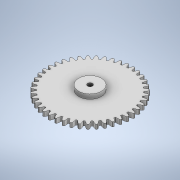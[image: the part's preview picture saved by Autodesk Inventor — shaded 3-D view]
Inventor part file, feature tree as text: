
AUTODESK INVENTOR PART (.ipt)
format: ipt  version: 2020 (Build 240168000, 168)  size: 538,112 bytes
history: native  units: mm
features: sketch x3, extrude x2, fillet x1, pattern_circular x1, hole x1
ambient origin geometry x8: Origin, YZ Plane, XZ Plane, XY Plane, X Axis, Y Axis, Z Axis, Center Point
bodies: Solid1 (feature_tree)
feature tree (8):
  extrude  "Extrusion1"  Depth=3.0mm TaperAngle=360.0deg
  fillet  "Fillet2"  Radius=53.2mm
  pattern_circular  "Circular Pattern2"  [2 undecoded]
  extrude  "Extrusion3"  Depth=3.0mm
  hole  "Hole1"  [1 undecoded]
  sketch  "Sketch1"  dims[d4=3.0mm d5=0.0mm d18=430.0mm d19=360.0deg d23=53.2mm]
  sketch  "Sketch3"  dims[d25=1.546512mm]
  sketch  "Sketch4"  dims[d26=1.237209mm d27=3.490659mm d28=49.991647mm d29=3.490659mm d30=0.309302mm d31=0.618605mm d32=0.971704mm d33=0.4mm d34=15.0mm d35=3.0mm d36=0.0mm d37=3.242mm d38=8.0mm d39=4.0mm d40=2.0mm d41=90.0deg d42=11.8mm d43=20.594885mm]
note: 3 required parameter values undecoded (feature->parameter linkage not recoverable at this tier; creation-order binding heuristic only, values carry confidence <= 0.55)
